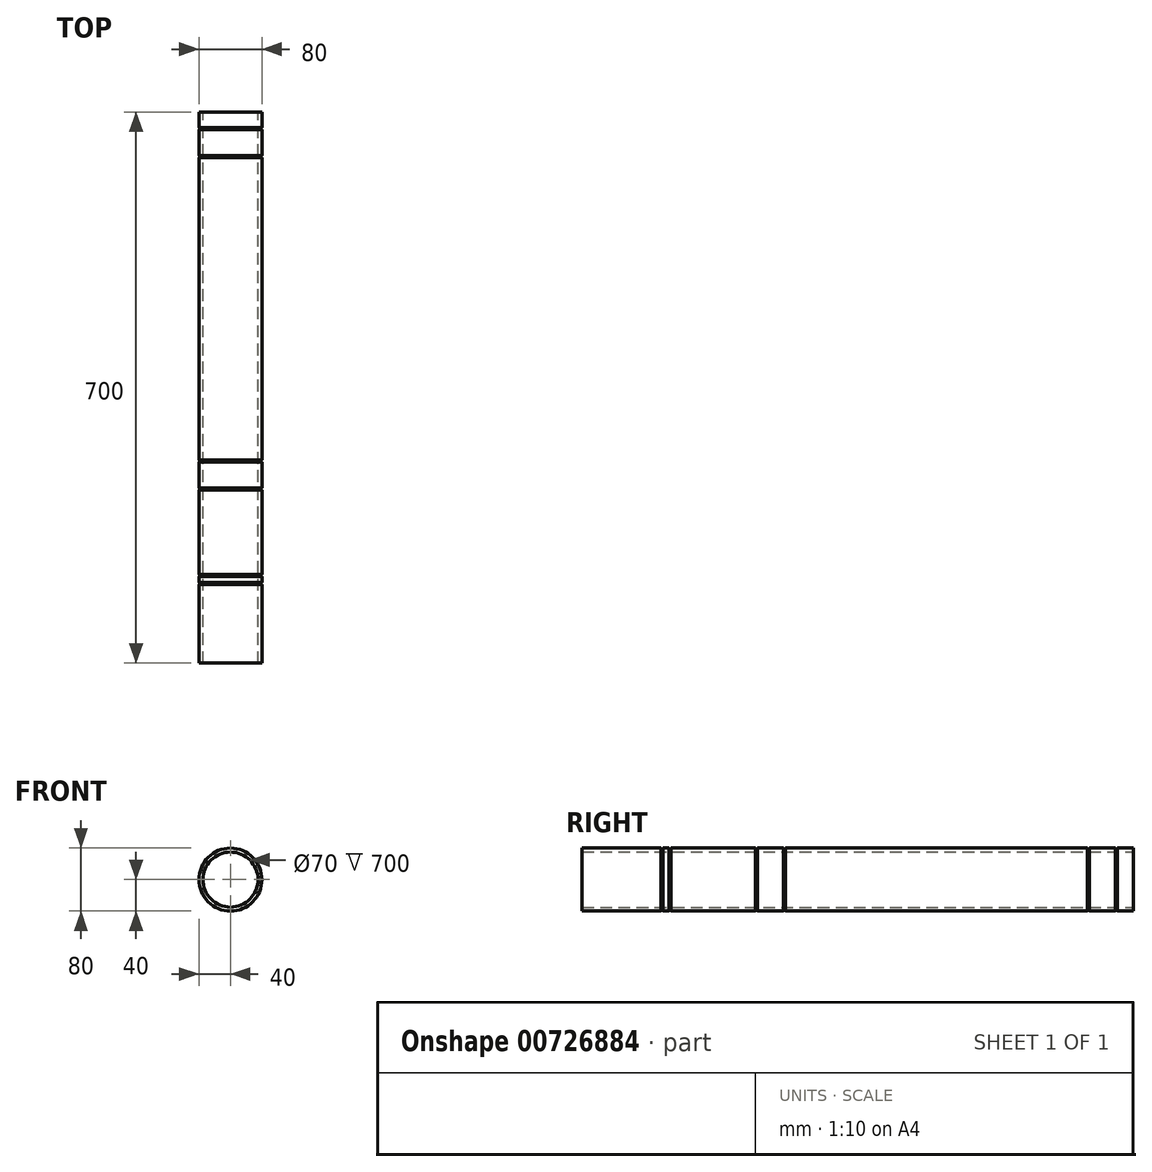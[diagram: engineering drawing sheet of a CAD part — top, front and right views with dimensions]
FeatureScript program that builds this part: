
annotation { "Feature Type Name" : "Feature", "Feature Type Description" : "" }
export const myFeature = defineFeature(function(context is Context, id is Id, definition is map)
    precondition{}
    {
        {
            var Q0;
            Q0=qCreatedBy(makeId("Front.planeOp"),FACE);
            var sketch = newSketch(context, id + "F0", { "sketchPlane" : qUnion([Q0])});
            skCircle(sketch, "E0", {"center": v(0, 0) * mm, "radius": 40 * mm});
            skCircle(sketch, "E1", {"center": v(0, 0) * mm, "radius": 35 * mm});
            skSolve(sketch);
        }
        {
            var Q0;
            Q0=makeQuery(id+"F0.imprint","IMPRINT",FACE,{"disambiguationData":[TD([[makeQuery(id+"F0.imprint","IMPRINT",EDGE,{"derivedFrom":sQuery(id+"F0.wireOp",EDGE,"E0")}),1.0]])]});
            extrude(context, id + "F1", {"entities" : qUnion([Q0]), "depth" : 700 * mm, "offsetDistance" : 25 * mm});
        }
        {
            var Q0;
            Q0=qCreatedBy(makeId("Front.planeOp"),FACE);
            cPlane(context, id + "F2", {"entities" : qUnion([Q0]), "cplaneType" : CPlaneType.OFFSET, "offset" : 20 * mm, "width" : 150 * mm, "height" : 150 * mm});
        }
        {
            var Q0;
            Q0=qCreatedBy(id+"F2.planeOp",FACE);
            var sketch = newSketch(context, id + "F3", { "sketchPlane" : qUnion([Q0])});
            skCircle(sketch, "E2", {"center": v(0, 0) * mm, "radius": 39.15 * mm});
            skCircle(sketch, "E3", {"center": v(0, 0) * mm, "radius": 44 * mm});
            skSolve(sketch);
        }
        {
            var Q0;
            Q0 = qSketchRegion(id + "F3", true);
            extrude(context, id + "F4", {"entities" : qUnion([Q0]), "operationType" : NewBodyOperationType.REMOVE, "depth" : 2.5 * mm, "offsetDistance" : 25 * mm});
        }
        {
            var Q0;
            Q0=qCreatedBy(id+"F2.planeOp",FACE);
            cPlane(context, id + "F5", {"entities" : qUnion([Q0]), "cplaneType" : CPlaneType.OFFSET, "offset" : 35.5 * mm, "width" : 150 * mm, "height" : 150 * mm});
        }
        {
            var Q0;
            Q0=qCreatedBy(id+"F5.planeOp",FACE);
            var sketch = newSketch(context, id + "F6", { "sketchPlane" : qUnion([Q0])});
            skCircle(sketch, "E4", {"center": v(0, 0) * mm, "radius": 39.15 * mm});
            skCircle(sketch, "E5", {"center": v(0, 0) * mm, "radius": 42.5 * mm});
            skSolve(sketch);
        }
        {
            var Q0;
            Q0 = qSketchRegion(id + "F6", true);
            extrude(context, id + "F7", {"entities" : qUnion([Q0]), "operationType" : NewBodyOperationType.REMOVE, "depth" : 2.5 * mm, "offsetDistance" : 25 * mm});
        }
        {
            var Q0;
            Q0=qCreatedBy(id+"F5.planeOp",FACE);
            cPlane(context, id + "F8", {"entities" : qUnion([Q0]), "cplaneType" : CPlaneType.OFFSET, "offset" : 444.5 * mm, "width" : 150 * mm, "height" : 150 * mm});
        }
        {
            var Q0;
            Q0=qCreatedBy(id+"F8.planeOp",FACE);
            cPlane(context, id + "F9", {"entities" : qUnion([Q0]), "cplaneType" : CPlaneType.OFFSET, "offset" : 20 * mm, "oppositeDirection" : true, "width" : 150 * mm, "height" : 150 * mm});
        }
        {
            var Q0;
            Q0=qCreatedBy(id+"F9.planeOp",FACE);
            var sketch = newSketch(context, id + "F10", { "sketchPlane" : qUnion([Q0])});
            skCircle(sketch, "E6", {"center": v(0, 0) * mm, "radius": 39.15 * mm});
            skCircle(sketch, "E7", {"center": v(0, 0) * mm, "radius": 42.5 * mm});
            skSolve(sketch);
        }
        {
            var Q0;
            Q0 = qSketchRegion(id + "F10", true);
            extrude(context, id + "F11", {"entities" : qUnion([Q0]), "operationType" : NewBodyOperationType.REMOVE, "oppositeDirection" : true, "depth" : 2.5 * mm, "offsetDistance" : 25 * mm});
        }
        {
            var Q0;
            Q0=qCreatedBy(id+"F9.planeOp",FACE);
            cPlane(context, id + "F12", {"entities" : qUnion([Q0]), "cplaneType" : CPlaneType.OFFSET, "offset" : 35.5 * mm, "oppositeDirection" : true, "width" : 150 * mm, "height" : 150 * mm});
        }
        {
            var Q0;
            Q0=qCreatedBy(id+"F12.planeOp",FACE);
            var sketch = newSketch(context, id + "F13", { "sketchPlane" : qUnion([Q0])});
            skCircle(sketch, "E8", {"center": v(0, 0) * mm, "radius": 39.15 * mm});
            skCircle(sketch, "E9", {"center": v(0, 0) * mm, "radius": 42.5 * mm});
            skSolve(sketch);
        }
        {
            var Q0;
            Q0 = qSketchRegion(id + "F13", true);
            extrude(context, id + "F14", {"entities" : qUnion([Q0]), "operationType" : NewBodyOperationType.REMOVE, "oppositeDirection" : true, "depth" : 2.5 * mm, "offsetDistance" : 25 * mm});
        }
        {
            var Q0;
            Q0=qCreatedBy(makeId("Front.planeOp"),FACE);
            cPlane(context, id + "F15", {"entities" : qUnion([Q0]), "cplaneType" : CPlaneType.OFFSET, "offset" : 590 * mm, "width" : 150 * mm, "height" : 150 * mm});
        }
        {
            var Q0;
            Q0=qCreatedBy(id+"F15.planeOp",FACE);
            var sketch = newSketch(context, id + "F16", { "sketchPlane" : qUnion([Q0])});
            skCircle(sketch, "E10", {"center": v(0, 0) * mm, "radius": 39.15 * mm});
            skCircle(sketch, "E11", {"center": v(0, 0) * mm, "radius": 44 * mm});
            skSolve(sketch);
        }
        {
            var Q0;
            Q0 = qSketchRegion(id + "F16", true);
            extrude(context, id + "F17", {"entities" : qUnion([Q0]), "operationType" : NewBodyOperationType.REMOVE, "oppositeDirection" : true, "depth" : 2.5 * mm, "offsetDistance" : 25 * mm});
        }
        {
            var Q0;
            Q0=qCreatedBy(id+"F15.planeOp",FACE);
            cPlane(context, id + "F18", {"entities" : qUnion([Q0]), "cplaneType" : CPlaneType.OFFSET, "offset" : 10 * mm, "width" : 150 * mm, "height" : 150 * mm});
        }
        {
            var Q0;
            Q0=qCreatedBy(id+"F18.planeOp",FACE);
            var sketch = newSketch(context, id + "F19", { "sketchPlane" : qUnion([Q0])});
            skCircle(sketch, "E12", {"center": v(0, 0) * mm, "radius": 39.15 * mm});
            skCircle(sketch, "E13", {"center": v(0, 0) * mm, "radius": 44 * mm});
            skSolve(sketch);
        }
        {
            var Q0;
            Q0 = qSketchRegion(id + "F19", true);
            extrude(context, id + "F20", {"entities" : qUnion([Q0]), "operationType" : NewBodyOperationType.REMOVE, "oppositeDirection" : true, "depth" : 2.5 * mm, "offsetDistance" : 25 * mm});
        }
    });
